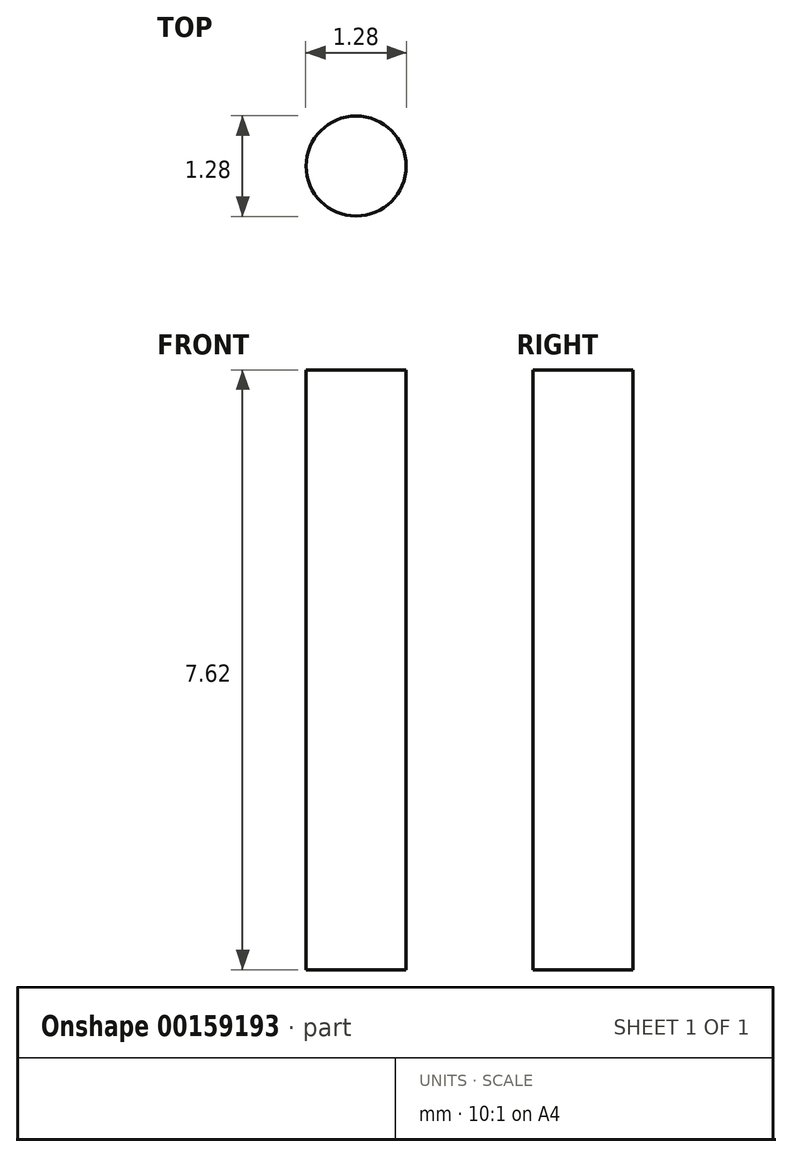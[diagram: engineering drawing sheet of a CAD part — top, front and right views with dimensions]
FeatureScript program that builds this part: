
annotation { "Feature Type Name" : "Feature", "Feature Type Description" : "" }
export const myFeature = defineFeature(function(context is Context, id is Id, definition is map)
    precondition{}
    {
        {
            var Q0;
            Q0=qCreatedBy(makeId("Top.planeOp"),FACE);
            var sketch = newSketch(context, id + "F0", { "sketchPlane" : qUnion([Q0])});
            skCircle(sketch, "E0", {"center": v(0, 0) * mm, "radius": 0.64 * mm});
            skSolve(sketch);
        }
        {
            var Q0;
            Q0=makeQuery(id+"F0.imprint","IMPRINT",FACE,{"disambiguationData":[TD([[makeQuery(id+"F0.imprint","IMPRINT",EDGE,{"derivedFrom":sQuery(id+"F0.wireOp",EDGE,"E0")}),1.0]])]});
            extrude(context, id + "F1", {"entities" : qUnion([Q0]), "depth" : 7.62 * mm});
        }
    });
